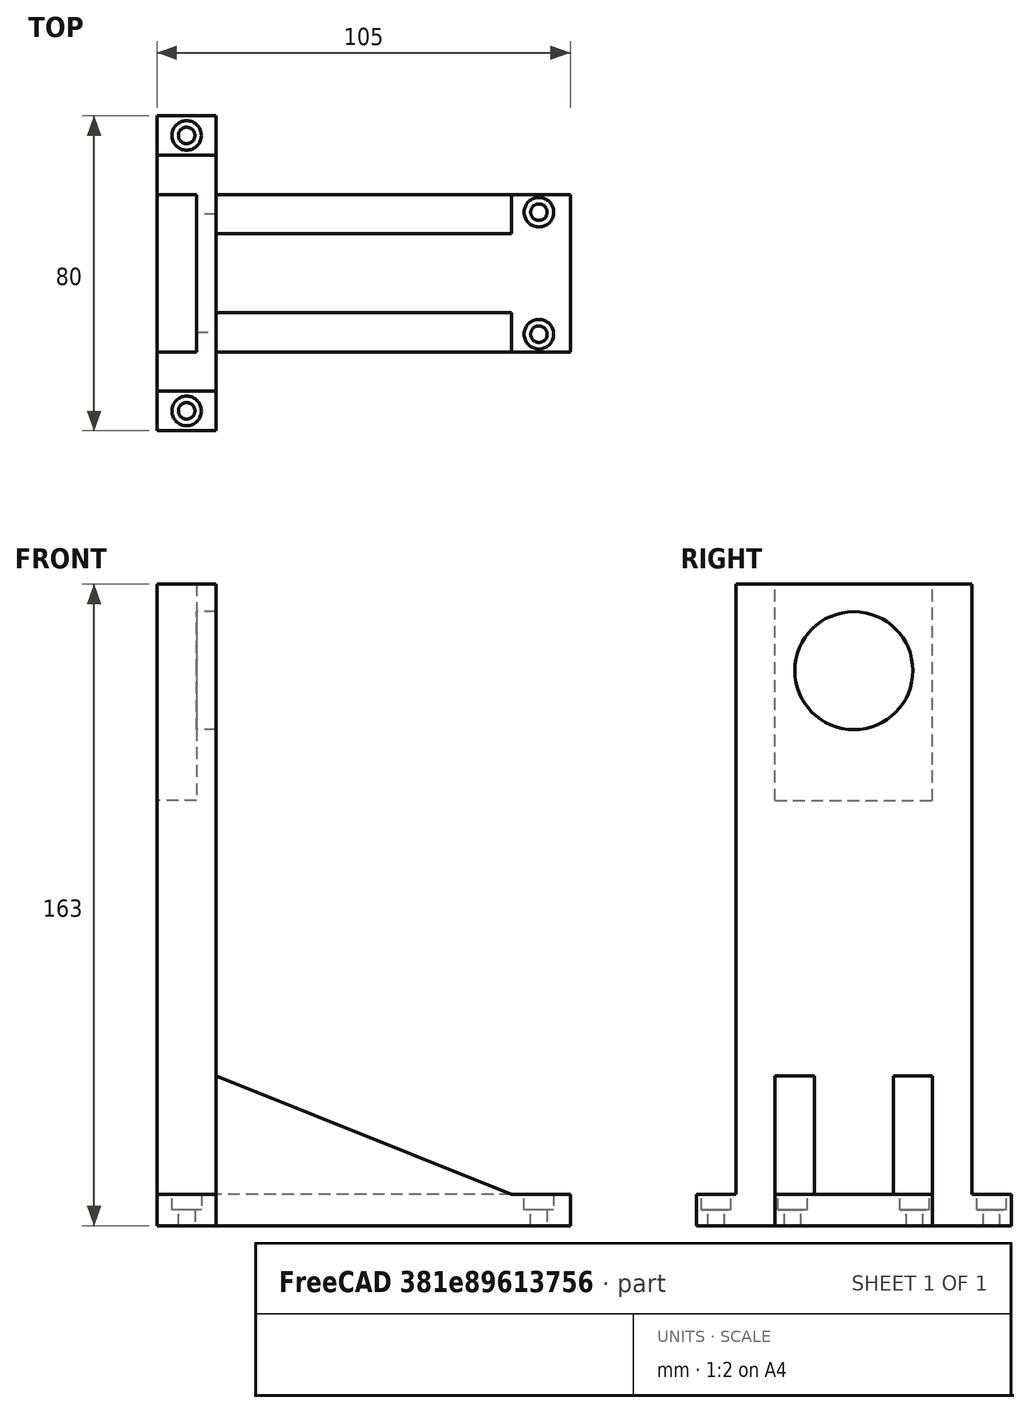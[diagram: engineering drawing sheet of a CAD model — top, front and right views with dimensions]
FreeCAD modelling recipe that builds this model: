
FCSTD DOCUMENT  (FreeCAD 2023.521R14555 (Git shallow))
Label: Filament_mount
License: All rights reserved
LicenseURL: https://en.wikipedia.org/wiki/All_rights_reserved
objects: Sketcher::SketchObject×7, TechDraw::DrawViewDimension×7, PartDesign::Pocket×4, PartDesign::Pad×3, PartDesign::Mirrored×2, PartDesign::Body×1, TechDraw::DrawSVGTemplate×1, TechDraw::DrawViewAnnotation×1, TechDraw::DrawViewPart×1, TechDraw::DrawRichAnno×1, TechDraw::DrawPage×1
note: 42 computed .brp shape members not serialized (recipe doc carries the construction recipe); baked Part::Feature solids carry a one-line shape summary decoded from their .brp

FEATURE [Sketcher::SketchObject] Sketch
  ArcFitTolerance = 1e-06
  AttachmentSupport = -> [XZ_Plane]
  ExternalBSplineMaxDegree = 5
  ExternalBSplineTolerance = 0.0001
  FixShape = 1
  FullyConstrained = true
  InternalTolerance = 1e-06
  InvalidShape = false
  MakeInternals = false
  MapMode = 5
  Placement = pos=(0,0,0) rot=(1,0,0;1.5708rad)
  Support = -> [XZ_Plane]
  TreeRank = 11
  ValidateShape = false
  sketch-geometry (6):
    g0: LineSegment StartX=0 StartY=163 StartZ=0 EndX=0 EndY=0 EndZ=0
    g1: LineSegment StartX=0 StartY=0 StartZ=0 EndX=105 EndY=-2e-16 EndZ=0
    g2: LineSegment StartX=105 StartY=-2e-16 StartZ=0 EndX=105 EndY=8 EndZ=0
    g3: LineSegment StartX=105 StartY=8 StartZ=0 EndX=15 EndY=8 EndZ=0
    g4: LineSegment StartX=15 StartY=8 StartZ=0 EndX=15 EndY=163 EndZ=0
    g5: LineSegment StartX=15 StartY=163 StartZ=0 EndX=0 EndY=163 EndZ=0
  constraints (17):
    c: PointOnObject(g0,g-2)
    c: Coincident(g0,g-1)
    c: Coincident(g1,g0)
    c: PointOnObject(g1,g-1)
    c: Coincident(g2,g1)
    c: Vertical(g2)
    c: Coincident(g3,g2)
    c: Horizontal(g3)
    c: Coincident(g4,g3)
    c: Vertical(g4)
    c: Coincident(g5,g4)
    c: Coincident(g5,g0)
    c: Horizontal(g5)
    c: DistanceX(g1,g1) = 105
    c: DistanceY(g2,g2) = 8
    c: DistanceX(g5,g5) = 15
    c: DistanceY(g4,g4) = 155
FEATURE [PartDesign::Pad] Pad
  AddSubType = 0
  AlongSketchNormal = false
  AutoTaperInnerAngle = true
  CheckUpToFaceLimits = true
  ClaimChildren = false
  Direction = (0,-1,2e-16)
  Fit = 0
  FitJoin = 0
  FixShape = 1
  InnerFit = 0
  InnerFitJoin = 0
  InvalidShape = false
  Length = 40
  Length2 = 10
  Linearize = true
  Midplane = true
  NewSolid = false
  Profile = -> Sketch
  ReferenceAxis = -> Sketch [N_Axis]
  Refine = true
  Suppress = false
  TaperInnerAngle = 0
  TaperInnerAngleRev = 0
  TreeRank = 12
  Type = 0
  ValidateShape = true
  _ProfileBasedVersion = 1
FEATURE [Sketcher::SketchObject] Sketch001
  ArcFitTolerance = 1e-06
  AttachmentSupport = -> [Pad]
  ExternalBSplineMaxDegree = 5
  ExternalBSplineTolerance = 0.0001
  ExternalGeometry = -> [Pad]
  FixShape = 1
  FullyConstrained = true
  InternalTolerance = 1e-06
  InvalidShape = false
  MakeInternals = false
  MapMode = 5
  Placement = pos=(0,-20,4.4e-15) rot=(1,0,0;1.5708rad)
  Support = -> [Pad]
  TreeRank = 13
  ValidateShape = false
  sketch-geometry (3):
    g0: LineSegment StartX=15 StartY=38 StartZ=0 EndX=90 EndY=8 EndZ=0
    g1: LineSegment StartX=90 StartY=8 StartZ=0 EndX=15 EndY=8 EndZ=0
    g2: LineSegment StartX=15 StartY=38 StartZ=0 EndX=15 EndY=8 EndZ=0
  constraints (8):
    c: PointOnObject(g0,g-4)
    c: PointOnObject(g0,g-3)
    c: Coincident(g1,g0)
    c: Coincident(g1,g-4)
    c: Coincident(g2,g0)
    c: Coincident(g2,g1)
    c: DistanceX(g1,g1) = 75
    c: DistanceY(g2,g2) = 30
FEATURE [PartDesign::Pad] Pad001
  AddSubType = 0
  AlongSketchNormal = false
  AutoTaperInnerAngle = true
  BaseFeature = -> Pad
  CheckUpToFaceLimits = true
  ClaimChildren = false
  Direction = (0,-1,2e-16)
  Fit = 0
  FitJoin = 0
  FixShape = 1
  InnerFit = 0
  InnerFitJoin = 0
  InvalidShape = false
  Length = 10
  Length2 = 10
  Linearize = true
  NewSolid = false
  Profile = -> Sketch001
  ReferenceAxis = -> Sketch001 [N_Axis]
  Refine = true
  Reversed = true
  Suppress = false
  TaperInnerAngle = 0
  TaperInnerAngleRev = 0
  TreeRank = 14
  Type = 0
  ValidateShape = true
  _ProfileBasedVersion = 1
FEATURE [PartDesign::Mirrored] Mirrored
  AddSubType = 0
  BaseFeature = -> Pad001
  CopyShape = false
  FixShape = 1
  InvalidShape = false
  MirrorPlane = -> XZ_Plane
  NewSolid = false
  OriginalSubs = -> [Pad001]
  Originals = -> [Pad001]
  ParallelTransform = true
  Refine = true
  SubTransform = true
  Suppress = false
  TreeRank = 15
  ValidateShape = true
  _Version = 3
FEATURE [Sketcher::SketchObject] Sketch002
  ArcFitTolerance = 1e-06
  AttachmentSupport = -> [Mirrored]
  ExternalBSplineMaxDegree = 5
  ExternalBSplineTolerance = 0.0001
  ExternalGeometry = -> [Mirrored]
  FixShape = 1
  FullyConstrained = true
  InternalTolerance = 1e-06
  InvalidShape = false
  MakeInternals = false
  MapMode = 5
  Placement = pos=(0,0,0) rot=(0.57735,-0.57735,-0.57735;2.0944rad)
  Support = -> [Mirrored]
  TreeRank = 16
  ValidateShape = false
  sketch-geometry (6):
    g0: LineSegment StartX=-40 StartY=0 StartZ=0 EndX=-20 EndY=0 EndZ=0
    g1: LineSegment StartX=-20 StartY=163 StartZ=0 EndX=-20 EndY=0 EndZ=0
    g2: LineSegment StartX=-30 StartY=8 StartZ=0 EndX=-40 EndY=8 EndZ=0
    g3: LineSegment StartX=-40 StartY=8 StartZ=0 EndX=-40 EndY=0 EndZ=0
    g4: LineSegment StartX=-30 StartY=8 StartZ=0 EndX=-30 EndY=163 EndZ=0
    g5: LineSegment StartX=-30 StartY=163 StartZ=0 EndX=-20 EndY=163 EndZ=0
  constraints (17):
    c: Horizontal(g0)
    c: Coincident(g0,g1)
    c: Vertical(g1)
    c: PointOnObject(g0,g-1)
    c: Vertical(g3)
    c: Coincident(g0,g3)
    c: Coincident(g2,g3)
    c: DistanceX(g2,g2) = 10
    c: Horizontal(g2)
    c: DistanceX(g2,g-1) = 40
    c: Vertical(g4)
    c: Coincident(g5,g1)
    c: Horizontal(g5)
    c: Coincident(g4,g5)
    c: Coincident(g1,g-3)
    c: Coincident(g2,g4)
    c: Horizontal(g2,g-4)
FEATURE [PartDesign::Pad] Pad002
  AddSubType = 0
  AlongSketchNormal = false
  AutoTaperInnerAngle = true
  BaseFeature = -> Mirrored
  CheckUpToFaceLimits = true
  ClaimChildren = false
  Direction = (-1,0,0)
  Fit = 0
  FitJoin = 0
  FixShape = 1
  InnerFit = 0
  InnerFitJoin = 0
  InvalidShape = false
  Length = 15
  Length2 = 10
  Linearize = true
  NewSolid = false
  Profile = -> Sketch002
  ReferenceAxis = -> Sketch002 [N_Axis]
  Refine = true
  Reversed = true
  Suppress = false
  TaperInnerAngle = 0
  TaperInnerAngleRev = 0
  TreeRank = 17
  Type = 0
  ValidateShape = true
  _ProfileBasedVersion = 1
FEATURE [PartDesign::Mirrored] Mirrored001
  AddSubType = 0
  BaseFeature = -> Pad002
  CopyShape = false
  FixShape = 1
  InvalidShape = false
  MirrorPlane = -> Sketch002 [V_Axis]
  NewSolid = false
  OriginalSubs = -> [Pad002]
  Originals = -> [Pad002]
  ParallelTransform = true
  Refine = true
  SubTransform = true
  Suppress = false
  TreeRank = 18
  ValidateShape = true
  _Version = 3
FEATURE [Sketcher::SketchObject] Sketch003
  ArcFitTolerance = 1e-06
  AttachmentSupport = -> [Mirrored001]
  ExternalBSplineMaxDegree = 5
  ExternalBSplineTolerance = 0.0001
  ExternalGeometry = -> [Mirrored001]
  FixShape = 1
  FullyConstrained = true
  InternalTolerance = 1e-06
  InvalidShape = false
  MakeInternals = false
  MapMode = 5
  Placement = pos=(0,1.8e-15,8) rot=(0,0,1;0rad)
  Support = -> [Mirrored001]
  TreeRank = 19
  ValidateShape = false
  sketch-geometry (5):
    g0: Circle CenterX=7.5 CenterY=35 CenterZ=0 NormalX=0 NormalY=0 NormalZ=1 AngleXU=0 Radius=2.1
    g1: Circle CenterX=7.5 CenterY=-35 CenterZ=0 NormalX=0 NormalY=0 NormalZ=1 AngleXU=0 Radius=2.1
    g2: Circle CenterX=97 CenterY=15.5 CenterZ=0 NormalX=0 NormalY=0 NormalZ=1 AngleXU=0 Radius=2.1
    g3: Circle CenterX=97 CenterY=-15.5 CenterZ=0 NormalX=0 NormalY=0 NormalZ=1 AngleXU=0 Radius=2.1
    g4: GeomPoint [constr] X=7.5 Y=40 Z=0
  constraints (11):
    c: Equal(g0,g1)
    c: Equal(g1,g2)
    c: Equal(g2,g3)
    c: Diameter(g1) = 4.2
    c: Symmetric(g1,g0,g-1)
    c: Symmetric(g2,g3,g-1)
    c: DistanceY(g3,g2) = 31
    c: DistanceY(g1,g0) = 70
    c: DistanceX(g2,g-3) = 8
    c: Symmetric(g-4,g-4,g4)
    c: Vertical(g0,g4)
FEATURE [PartDesign::Pocket] Pocket
  AddSubType = 1
  AlongSketchNormal = false
  AutoTaperInnerAngle = true
  BaseFeature = -> Mirrored001
  CheckUpToFaceLimits = true
  ClaimChildren = false
  Direction = (0,-2e-16,-1)
  Fit = 0
  FitJoin = 0
  FixShape = 1
  InnerFit = 0
  InnerFitJoin = 0
  InvalidShape = false
  Length = 5
  Length2 = 10
  Linearize = true
  NewSolid = false
  Profile = -> Sketch003
  ReferenceAxis = -> Sketch003 [N_Axis]
  Refine = true
  Suppress = false
  TaperInnerAngle = 0
  TaperInnerAngleRev = 0
  TreeRank = 20
  Type = 1
  ValidateShape = true
  _ProfileBasedVersion = 1
  _Version = 1
FEATURE [Sketcher::SketchObject] Sketch004
  ArcFitTolerance = 1e-06
  AttachmentSupport = -> [Pocket]
  ExternalBSplineMaxDegree = 5
  ExternalBSplineTolerance = 0.0001
  ExternalGeometry = -> [Pocket]
  FixShape = 1
  FullyConstrained = true
  InternalTolerance = 1e-06
  InvalidShape = false
  MakeInternals = false
  MapMode = 5
  Placement = pos=(0,1.8e-15,8) rot=(0,0,1;0rad)
  Support = -> [Pocket]
  TreeRank = 21
  ValidateShape = false
  sketch-geometry (4):
    g0: Circle CenterX=7.5 CenterY=35 CenterZ=0 NormalX=0 NormalY=0 NormalZ=1 AngleXU=0 Radius=3.75
    g1: Circle CenterX=97 CenterY=15.5 CenterZ=0 NormalX=0 NormalY=0 NormalZ=1 AngleXU=0 Radius=3.75
    g2: Circle CenterX=97 CenterY=-15.5 CenterZ=0 NormalX=0 NormalY=0 NormalZ=1 AngleXU=0 Radius=3.75
    g3: Circle CenterX=7.5 CenterY=-35 CenterZ=0 NormalX=0 NormalY=0 NormalZ=1 AngleXU=0 Radius=3.75
  constraints (8):
    c: Coincident(g0,g-6)
    c: Coincident(g1,g-5)
    c: Coincident(g2,g-4)
    c: Coincident(g3,g-3)
    c: Equal(g0,g1)
    c: Equal(g1,g2)
    c: Equal(g2,g3)
    c: Diameter(g3) = 7.5
FEATURE [PartDesign::Pocket] Pocket001
  AddSubType = 1
  AlongSketchNormal = false
  AutoTaperInnerAngle = true
  BaseFeature = -> Pocket
  CheckUpToFaceLimits = true
  ClaimChildren = false
  Direction = (0,-2e-16,-1)
  Fit = 0
  FitJoin = 0
  FixShape = 1
  InnerFit = 0
  InnerFitJoin = 0
  InvalidShape = false
  Length = 4
  Length2 = 10
  Linearize = true
  NewSolid = false
  Profile = -> Sketch004
  ReferenceAxis = -> Sketch004 [N_Axis]
  Refine = true
  Suppress = false
  TaperInnerAngle = 0
  TaperInnerAngleRev = 0
  TreeRank = 22
  Type = 0
  ValidateShape = true
  _ProfileBasedVersion = 1
  _Version = 1
FEATURE [Sketcher::SketchObject] Sketch005
  ArcFitTolerance = 1e-06
  AttachmentSupport = -> [Pocket001]
  ExternalBSplineMaxDegree = 5
  ExternalBSplineTolerance = 0.0001
  ExternalGeometry = -> [Pocket001]
  FixShape = 1
  FullyConstrained = true
  InternalTolerance = 1e-06
  InvalidShape = false
  MakeInternals = false
  MapMode = 5
  Placement = pos=(-1e-16,-20,4.4e-15) rot=(1,0,0;1.5708rad)
  Support = -> [Pocket001]
  TreeRank = 23
  ValidateShape = false
  sketch-geometry (4):
    g0: LineSegment StartX=0 StartY=163 StartZ=0 EndX=10 EndY=163 EndZ=0
    g1: LineSegment StartX=10 StartY=163 StartZ=0 EndX=10 EndY=108 EndZ=0
    g2: LineSegment StartX=10 StartY=108 StartZ=0 EndX=0 EndY=108 EndZ=0
    g3: LineSegment StartX=0 StartY=108 StartZ=0 EndX=0 EndY=163 EndZ=0
  constraints (11):
    c: Coincident(g0,g1)
    c: Coincident(g1,g2)
    c: Coincident(g2,g3)
    c: Coincident(g3,g0)
    c: Horizontal(g0)
    c: Horizontal(g2)
    c: Vertical(g1)
    c: Vertical(g3)
    c: DistanceY(g1,g1) = 55
    c: Coincident(g0,g-3)
    c: DistanceX(g0,g-4) = 5
FEATURE [PartDesign::Pocket] Pocket002
  AddSubType = 1
  AlongSketchNormal = false
  AutoTaperInnerAngle = true
  BaseFeature = -> Pocket001
  CheckUpToFaceLimits = true
  ClaimChildren = false
  Direction = (0,1,-2e-16)
  Fit = 0
  FitJoin = 0
  FixShape = 1
  InnerFit = 0
  InnerFitJoin = 0
  InvalidShape = false
  Length = 0
  Length2 = 10
  Linearize = true
  NewSolid = false
  Profile = -> Sketch005
  ReferenceAxis = -> Sketch005 [N_Axis]
  Refine = true
  Suppress = false
  TaperInnerAngle = 0
  TaperInnerAngleRev = 0
  TreeRank = 24
  Type = 3
  UpToFace = -> Pocket001 [Face18]
  ValidateShape = true
  _ProfileBasedVersion = 1
  _Version = 1
FEATURE [Sketcher::SketchObject] Sketch006
  ArcFitTolerance = 1e-06
  AttachmentSupport = -> [Pocket002]
  ExternalBSplineMaxDegree = 5
  ExternalBSplineTolerance = 0.0001
  ExternalGeometry = -> [Pocket002]
  FixShape = 1
  FullyConstrained = true
  InternalTolerance = 1e-06
  InvalidShape = false
  MakeInternals = false
  MapMode = 5
  Placement = pos=(10,-1e-16,0) rot=(-0.57735,0.57735,0.57735;4.18879rad)
  Support = -> [Pocket002]
  TreeRank = 25
  ValidateShape = false
  sketch-geometry (1):
    g0: Circle CenterX=0 CenterY=141 CenterZ=0 NormalX=0 NormalY=0 NormalZ=1 AngleXU=0 Radius=15
  constraints (3):
    c: PointOnObject(g0,g-2)
    c: Diameter(g0) = 30
    c: DistanceY(g0,g-3) = 22
FEATURE [PartDesign::Pocket] Pocket003
  AddSubType = 1
  AlongSketchNormal = false
  AutoTaperInnerAngle = true
  BaseFeature = -> Pocket002
  CheckUpToFaceLimits = true
  ClaimChildren = false
  Direction = (1,0,0)
  Fit = 0
  FitJoin = 0
  FixShape = 1
  InnerFit = 0
  InnerFitJoin = 0
  InvalidShape = false
  Length = 5
  Length2 = 10
  Linearize = true
  NewSolid = false
  Profile = -> Sketch006
  ReferenceAxis = -> Sketch006 [N_Axis]
  Refine = true
  Suppress = false
  TaperInnerAngle = 0
  TaperInnerAngleRev = 0
  TreeRank = 26
  Type = 1
  ValidateShape = true
  _ProfileBasedVersion = 1
  _Version = 1
FEATURE [PartDesign::Body] Body
  AutoGroupSolids = false
  ClaimAllChildren = false
  ExportMode = 0
  FixShape = 1
  Group = -> [Sketch,Pad,Sketch001,Pad001,Mirrored,Sketch002,Pad002,Mirrored001,Sketch003,Pocket,Sketch004,Pocket001,Sketch005,Pocket002,Sketch006,Pocket003]
  InvalidShape = false
  Origin = -> Origin
  Tip = -> Pocket003
  TreeRank = 10
  ValidateShape = false
  _ExportChildren = -> [Pad,Pad001,Mirrored,Pad002,Mirrored001,Pocket,Pocket001,Pocket002,Pocket003]
  _GroupVersion = 1
FEATURE [TechDraw::DrawSVGTemplate] Template
  EditableTexts = Approved1=Approved 1; Approved2=Approved 2; CheckedBy=Checked By; Code=Code; CompanyAddress=1234 Main St; CompanyName=Company Name; DrawingNumber=Drawing Number; DrawingTitle1=Drawing Title 1; DrawingTitle2=Drawing Title 2; DrawingTitle3=Drawing Title 3; DrawnBy=Drawn By; Revision=Rev; Scale=Scale; Sheet=Sheet n of m
  Height = 215.9
  Orientation = 1
  Template = /app/share/Mod/TechDraw/Templates/USLetter_Landscape.svg
  TreeRank = 28
  Width = 279.4
FEATURE [TechDraw::DrawViewAnnotation] Annotation
  Font = osifont
  LineSpace = 80
  LockPosition = false
  MaxWidth = -1
  Rotation = 0
  ScaleType = 0
  Text = Front
  TextSize = 5
  TextStyle = 0
  TreeRank = 46
  X = 97.1616
  Y = 91.8772
FEATURE [TechDraw::DrawViewPart] View  label="Front"
  CoarseView = false
  Direction = (1,0,0)
  Focus = 100
  HardHidden = false
  IsoCount = 0
  IsoHidden = false
  IsoVisible = false
  LockPosition = false
  Perspective = false
  Rotation = 0
  ScaleType = 0
  SeamHidden = false
  SeamVisible = true
  SmoothHidden = false
  SmoothVisible = true
  Source = -> [Pocket003]
  TreeRank = 63
  X = 148.111
  XDirection = (0,0,-1)
  Y = 130.477
FEATURE [TechDraw::DrawRichAnno] RichTextAnnotation
  AnnoParent = -> View
  AnnoText = <!DOCTYPE HTML PUBLIC "-//W3C//DTD HTML 4.0//EN" "http://www.w3.org/TR/REC-html40/strict.dtd">\n<html><head><meta name="qrichtext" content="1" /><style type="text/css">\np, li { white-space: pre-wrap; }\n</style></head><body style=" font-family:'Ubuntu'; font-size:11pt; font-weight:400; font-style:normal;">\n<p style=" margin-top:0px; margin-bottom:0px; margin-left:0px; margin-right:0px; -qt-block-indent:0; text-indent:0px;">Holds fillament rolll</p></body></html>
  LockPosition = false
  MaxWidth = -1
  Rotation = 0
  ScaleType = 0
  ShowFrame = false
  TreeRank = 47
  X = -87.9215
  Y = 57.5325
FEATURE [TechDraw::DrawViewDimension] Dimension002
  AngleOverride = false
  Arbitrary = false
  ArbitraryTolerances = false
  EqualTolerance = true
  ExtensionAngle = 0
  FormatSpec = ⌀%.2w
  FormatSpecOverTolerance = %+.2w
  FormatSpecUnderTolerance = %+.2w
  Inverted = false
  LineAngle = 0
  LockPosition = false
  MeasureType = 1
  OverTolerance = 0
  References2D = -> [View]
  Rotation = 0
  ScaleType = 0
  TheoreticalExact = false
  TreeRank = 56
  Type = 5
  UnderTolerance = 0
  X = -28.1681
  Y = -6.65079
FEATURE [TechDraw::DrawViewDimension] Dimension005
  AngleOverride = false
  Arbitrary = false
  ArbitraryTolerances = false
  EqualTolerance = true
  ExtensionAngle = 0
  FormatSpec = %.3w
  FormatSpecOverTolerance = %+.2w
  FormatSpecUnderTolerance = %+.2w
  Inverted = false
  LineAngle = 0
  LockPosition = false
  MeasureType = 1
  OverTolerance = 0
  References2D = -> [View]
  Rotation = 0
  ScaleType = 0
  TheoreticalExact = false
  TreeRank = 57
  Type = 2
  UnderTolerance = 0
  X = 66.0591
  Y = -44.6279
FEATURE [TechDraw::DrawViewDimension] Dimension001
  AngleOverride = false
  Arbitrary = false
  ArbitraryTolerances = false
  EqualTolerance = true
  ExtensionAngle = 0
  FormatSpec = %.2w
  FormatSpecOverTolerance = %+.2w
  FormatSpecUnderTolerance = %+.2w
  Inverted = false
  LineAngle = 0
  LockPosition = false
  MeasureType = 1
  OverTolerance = 0
  References2D = -> [View]
  Rotation = 0
  ScaleType = 0
  TheoreticalExact = false
  TreeRank = 58
  Type = 1
  UnderTolerance = 0
  X = 58.1011
  Y = 18.5878
FEATURE [TechDraw::DrawViewDimension] Dimension004
  AngleOverride = false
  Arbitrary = false
  ArbitraryTolerances = false
  EqualTolerance = true
  ExtensionAngle = 0
  FormatSpec = %.2w
  FormatSpecOverTolerance = %+.2w
  FormatSpecUnderTolerance = %+.2w
  Inverted = false
  LineAngle = 0
  LockPosition = false
  MeasureType = 1
  OverTolerance = 0
  References2D = -> [View]
  Rotation = 0
  ScaleType = 0
  TheoreticalExact = false
  TreeRank = 59
  Type = 2
  UnderTolerance = 0
  X = 36.0591
  Y = 0.0191409
FEATURE [TechDraw::DrawViewDimension] Dimension
  AngleOverride = false
  Arbitrary = false
  ArbitraryTolerances = false
  EqualTolerance = true
  ExtensionAngle = 0
  FormatSpec = %.2w
  FormatSpecOverTolerance = %+.2w
  FormatSpecUnderTolerance = %+.2w
  Inverted = false
  LineAngle = 0
  LockPosition = false
  MeasureType = 1
  OverTolerance = 0
  References2D = -> [View]
  Rotation = 0
  ScaleType = 0
  TheoreticalExact = false
  TreeRank = 60
  Type = 1
  UnderTolerance = 0
  X = -26.24
  Y = 45.5979
FEATURE [TechDraw::DrawViewDimension] Dimension006
  AngleOverride = false
  Arbitrary = false
  ArbitraryTolerances = false
  EqualTolerance = true
  ExtensionAngle = 0
  FormatSpec = %.2w
  FormatSpecOverTolerance = %+.2w
  FormatSpecUnderTolerance = %+.2w
  Inverted = false
  LineAngle = 0
  LockPosition = false
  MeasureType = 1
  OverTolerance = 0
  References2D = -> [View]
  Rotation = 0
  ScaleType = 0
  TheoreticalExact = false
  TreeRank = 61
  Type = 1
  UnderTolerance = 0
  X = -72.7363
  Y = -1.90593
FEATURE [TechDraw::DrawViewDimension] Dimension003
  AngleOverride = false
  Arbitrary = false
  ArbitraryTolerances = false
  EqualTolerance = true
  ExtensionAngle = 0
  FormatSpec = %.2w
  FormatSpecOverTolerance = %+.2w
  FormatSpecUnderTolerance = %+.2w
  Inverted = false
  LineAngle = 0
  LockPosition = false
  MeasureType = 1
  OverTolerance = 0
  References2D = -> [View]
  Rotation = 0
  ScaleType = 0
  TheoreticalExact = false
  TreeRank = 62
  Type = 2
  UnderTolerance = 0
  X = 85.7958
  Y = 1.32633
FEATURE [TechDraw::DrawPage] Page
  KeepUpdated = true
  NextBalloonIndex = 1
  ProjectionType = 0
  Template = -> Template
  TreeRank = 29
  Views = -> [View,Dimension,Dimension001,Dimension002,Dimension003,Dimension004,Dimension005,Dimension006,Annotation,RichTextAnnotation]
